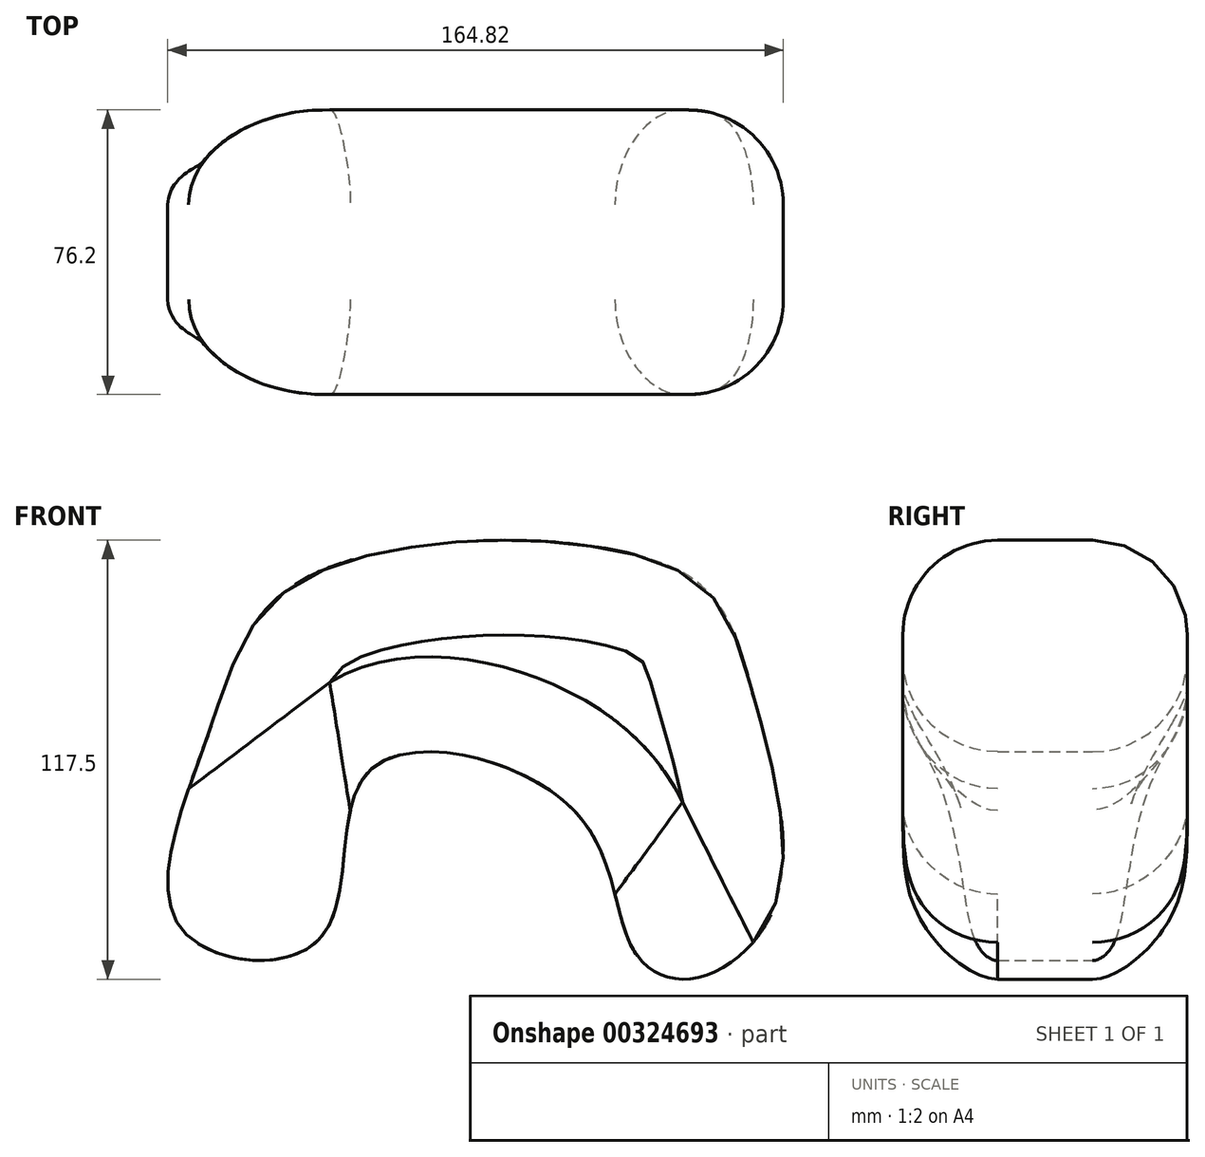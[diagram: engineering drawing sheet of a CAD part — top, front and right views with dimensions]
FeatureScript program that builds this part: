
annotation { "Feature Type Name" : "Feature", "Feature Type Description" : "" }
export const myFeature = defineFeature(function(context is Context, id is Id, definition is map)
    precondition{}
    {
        {
            var Q0;
            Q0=qCreatedBy(makeId("Front.planeOp"),FACE);
            var sketch = newSketch(context, id + "F0", { "sketchPlane" : qUnion([Q0])});
            skFitSpline(sketch, "E0", {"points": [v(-72.12, -31.91) * mm, v(-64.86, 20.53) * mm, v(-37.98, 62.43) * mm, v(59.74, 64.61) * mm, v(80.24, 33.04) * mm, v(87.31, -23.9) * mm, v(64.77, -45.17) * mm, v(48.65, -37.16) * mm, v(32.75, 0) * mm, v(-21.75, 10.48) * mm, v(-35, -34.42) * mm, v(-72.12, -31.91) * mm]});
            skSolve(sketch);
        }
        {
            var Q0;
            Q0 = qSketchRegion(id + "F0", true);
            extrude(context, id + "F1", {"entities" : qUnion([Q0]), "depth" : 76.2 * mm});
        }
        {
            var Q0;
            Q0=makeQuery(id+"F1.opExtrude","SWEPT_FACE",FACE,{"disambiguationData":[OSD([sQuery(id+"F0.wireOp",EDGE,"E0")])]});
            fillet(context, id + "F2", {"entities" : qUnion([Q0]), "radius" : 25.4 * mm, "tangentPropagation" : true, "allowEdgeOverflow" : false});
        }
    });
